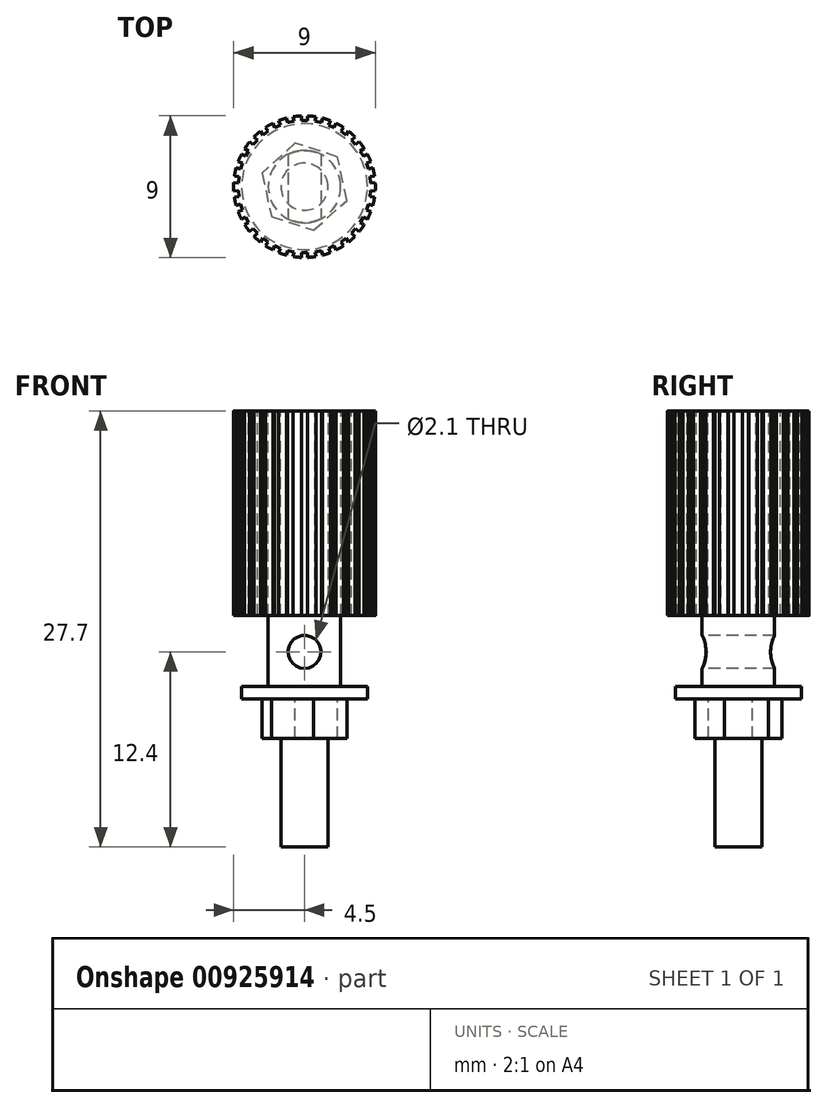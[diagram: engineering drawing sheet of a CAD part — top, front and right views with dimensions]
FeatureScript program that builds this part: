
annotation { "Feature Type Name" : "Feature", "Feature Type Description" : "" }
export const myFeature = defineFeature(function(context is Context, id is Id, definition is map)
    precondition{}
    {
        {
            var Q0;
            Q0=qCreatedBy(makeId("Top.planeOp"),FACE);
            var sketch = newSketch(context, id + "F0", { "sketchPlane" : qUnion([Q0])});
            skCircle(sketch, "E0", {"center": v(0, 0) * mm, "radius": 4 * mm});
            skSolve(sketch);
        }
        {
            var Q0;
            Q0 = qSketchRegion(id + "F0", true);
            extrude(context, id + "F1", {"entities" : qUnion([Q0]), "depth" : 0.8 * mm, "offsetDistance" : 25 * mm});
        }
        {
            var Q0;
            Q0=makeQuery(id+"F1.opExtrude","CAP_FACE",FACE,{"disambiguationData":[OSD([sQuery(id+"F0.wireOp",EDGE,"E0")])],"isStart":false});
            var sketch = newSketch(context, id + "F2", { "sketchPlane" : qUnion([Q0])});
            skCircle(sketch, "E1", {"center": v(0, 0) * mm, "radius": 2.3 * mm});
            skSolve(sketch);
        }
        {
            var Q0;
            Q0 = qSketchRegion(id + "F2", true);
            extrude(context, id + "F3", {"entities" : qUnion([Q0]), "operationType" : NewBodyOperationType.ADD, "depth" : 4.5 * mm, "offsetDistance" : 25 * mm});
        }
        {
            var Q0;
            Q0=makeQuery(id+"F3.opExtrude","CAP_FACE",FACE,{"disambiguationData":[OSD([sQuery(id+"F2.wireOp",EDGE,"E1")])],"isStart":false});
            var sketch = newSketch(context, id + "F4", { "sketchPlane" : qUnion([Q0])});
            skCircle(sketch, "E2", {"center": v(0, 0) * mm, "radius": 4.5 * mm});
            skSolve(sketch);
        }
        {
            var Q0;
            Q0 = qSketchRegion(id + "F4", true);
            extrude(context, id + "F5", {"entities" : qUnion([Q0]), "operationType" : NewBodyOperationType.ADD, "depth" : 13 * mm, "offsetDistance" : 25 * mm});
        }
        {
            var Q0;
            Q0=makeQuery(id+"F1.opExtrude","CAP_FACE",FACE,{"disambiguationData":[OSD([sQuery(id+"F0.wireOp",EDGE,"E0")])],"isStart":true});
            var sketch = newSketch(context, id + "F6", { "sketchPlane" : qUnion([Q0])});
            skCircle(sketch, "E3", {"center": v(0, 0) * mm, "radius": 1.5 * mm});
            skSolve(sketch);
        }
        {
            var Q0;
            Q0 = qSketchRegion(id + "F6", true);
            extrude(context, id + "F7", {"entities" : qUnion([Q0]), "operationType" : NewBodyOperationType.ADD, "depth" : 9.4 * mm, "offsetDistance" : 25 * mm});
        }
        {
            var Q0;
            Q0=qCreatedBy(makeId("Front.planeOp"),FACE);
            var sketch = newSketch(context, id + "F8", { "sketchPlane" : qUnion([Q0])});
            skCircle(sketch, "E4", {"center": v(0, 3) * mm, "radius": 1.05 * mm});
            skSolve(sketch);
        }
        {
            var Q0;
            Q0 = qSketchRegion(id + "F8", true);
            extrude(context, id + "F9", {"entities" : qUnion([Q0]), "operationType" : NewBodyOperationType.REMOVE, "oppositeDirection" : true, "depth" : 25 * mm, "offsetDistance" : 25 * mm, "symmetric" : true});
        }
        {
            var Q0;
            Q0=makeQuery(id+"F5.opExtrude","CAP_FACE",FACE,{"disambiguationData":[OSD([sQuery(id+"F4.wireOp",EDGE,"E2")])],"isStart":false});
            var sketch = newSketch(context, id + "F10", { "sketchPlane" : qUnion([Q0])});
            skLineSegment(sketch, "E5.bottom", {"start": v(0.2, 4.2) * mm, "end": v(-0.2, 4.2) * mm});
            skLineSegment(sketch, "E5.top", {"start": v(0.2, 4.8) * mm, "end": v(-0.2, 4.8) * mm});
            skLineSegment(sketch, "E5.left", {"start": v(0.2, 4.2) * mm, "end": v(0.2, 4.8) * mm});
            skLineSegment(sketch, "E5.right", {"start": v(-0.2, 4.2) * mm, "end": v(-0.2, 4.8) * mm});
            skPoint(sketch, "E5.middle", {"position": v(0, 4.5) * mm});
            skSolve(sketch);
        }
        {
            var Q0;
            Q0 = qSketchRegion(id + "F10", true);
            extrude(context, id + "F11", {"entities" : qUnion([Q0]), "oppositeDirection" : true, "depth" : 25 * mm, "offsetDistance" : 25 * mm});
        }
        {
            var Q0;
            Q0=makeQuery(id+"F11.opExtrude","SWEPT_BODY",BODY,{"disambiguationData":[OSD([sQuery(id+"F10.wireOp",EDGE,"E5.bottom"),sQuery(id+"F10.wireOp",EDGE,"E5.top"),sQuery(id+"F10.wireOp",EDGE,"E5.left"),sQuery(id+"F10.wireOp",EDGE,"E5.right")])]});
            var Q1;
            Q1=makeQuery(id+"F5.opExtrude","CAP_EDGE",EDGE,{"disambiguationData":[OSD([sQuery(id+"F4.wireOp",EDGE,"E2")])],"isStart":false});
            circularPattern(context, id + "F12", {"entities" : qUnion([Q0]), "axis" : qUnion([Q1]), "angle" : 360 * degree, "instanceCount" : 30, "equalSpace" : true});
        }
        {
            var Q0;
            Q0=makeQuery(id+"F12.opPattern","COPY",BODY,{"derivedFrom":makeQuery(id+"F11.opExtrude","SWEPT_BODY",BODY,{"disambiguationData":[OSD([sQuery(id+"F10.wireOp",EDGE,"E5.bottom"),sQuery(id+"F10.wireOp",EDGE,"E5.top"),sQuery(id+"F10.wireOp",EDGE,"E5.left"),sQuery(id+"F10.wireOp",EDGE,"E5.right")])]}),"instanceName":"1"});
            var Q1;
            Q1=makeQuery(id+"F12.opPattern","COPY",BODY,{"derivedFrom":makeQuery(id+"F11.opExtrude","SWEPT_BODY",BODY,{"disambiguationData":[OSD([sQuery(id+"F10.wireOp",EDGE,"E5.bottom"),sQuery(id+"F10.wireOp",EDGE,"E5.top"),sQuery(id+"F10.wireOp",EDGE,"E5.left"),sQuery(id+"F10.wireOp",EDGE,"E5.right")])]}),"instanceName":"2"});
            var Q2;
            Q2=makeQuery(id+"F12.opPattern","COPY",BODY,{"derivedFrom":makeQuery(id+"F11.opExtrude","SWEPT_BODY",BODY,{"disambiguationData":[OSD([sQuery(id+"F10.wireOp",EDGE,"E5.bottom"),sQuery(id+"F10.wireOp",EDGE,"E5.top"),sQuery(id+"F10.wireOp",EDGE,"E5.left"),sQuery(id+"F10.wireOp",EDGE,"E5.right")])]}),"instanceName":"3"});
            var Q3;
            Q3=makeQuery(id+"F12.opPattern","COPY",BODY,{"derivedFrom":makeQuery(id+"F11.opExtrude","SWEPT_BODY",BODY,{"disambiguationData":[OSD([sQuery(id+"F10.wireOp",EDGE,"E5.bottom"),sQuery(id+"F10.wireOp",EDGE,"E5.top"),sQuery(id+"F10.wireOp",EDGE,"E5.left"),sQuery(id+"F10.wireOp",EDGE,"E5.right")])]}),"instanceName":"4"});
            var Q4;
            Q4=makeQuery(id+"F12.opPattern","COPY",BODY,{"derivedFrom":makeQuery(id+"F11.opExtrude","SWEPT_BODY",BODY,{"disambiguationData":[OSD([sQuery(id+"F10.wireOp",EDGE,"E5.bottom"),sQuery(id+"F10.wireOp",EDGE,"E5.top"),sQuery(id+"F10.wireOp",EDGE,"E5.left"),sQuery(id+"F10.wireOp",EDGE,"E5.right")])]}),"instanceName":"5"});
            var Q5;
            Q5=makeQuery(id+"F12.opPattern","COPY",BODY,{"derivedFrom":makeQuery(id+"F11.opExtrude","SWEPT_BODY",BODY,{"disambiguationData":[OSD([sQuery(id+"F10.wireOp",EDGE,"E5.bottom"),sQuery(id+"F10.wireOp",EDGE,"E5.top"),sQuery(id+"F10.wireOp",EDGE,"E5.left"),sQuery(id+"F10.wireOp",EDGE,"E5.right")])]}),"instanceName":"6"});
            var Q6;
            Q6=makeQuery(id+"F12.opPattern","COPY",BODY,{"derivedFrom":makeQuery(id+"F11.opExtrude","SWEPT_BODY",BODY,{"disambiguationData":[OSD([sQuery(id+"F10.wireOp",EDGE,"E5.bottom"),sQuery(id+"F10.wireOp",EDGE,"E5.top"),sQuery(id+"F10.wireOp",EDGE,"E5.left"),sQuery(id+"F10.wireOp",EDGE,"E5.right")])]}),"instanceName":"7"});
            var Q7;
            Q7=makeQuery(id+"F12.opPattern","COPY",BODY,{"derivedFrom":makeQuery(id+"F11.opExtrude","SWEPT_BODY",BODY,{"disambiguationData":[OSD([sQuery(id+"F10.wireOp",EDGE,"E5.bottom"),sQuery(id+"F10.wireOp",EDGE,"E5.top"),sQuery(id+"F10.wireOp",EDGE,"E5.left"),sQuery(id+"F10.wireOp",EDGE,"E5.right")])]}),"instanceName":"8"});
            var Q8;
            Q8=makeQuery(id+"F12.opPattern","COPY",BODY,{"derivedFrom":makeQuery(id+"F11.opExtrude","SWEPT_BODY",BODY,{"disambiguationData":[OSD([sQuery(id+"F10.wireOp",EDGE,"E5.bottom"),sQuery(id+"F10.wireOp",EDGE,"E5.top"),sQuery(id+"F10.wireOp",EDGE,"E5.left"),sQuery(id+"F10.wireOp",EDGE,"E5.right")])]}),"instanceName":"9"});
            var Q9;
            Q9=makeQuery(id+"F12.opPattern","COPY",BODY,{"derivedFrom":makeQuery(id+"F11.opExtrude","SWEPT_BODY",BODY,{"disambiguationData":[OSD([sQuery(id+"F10.wireOp",EDGE,"E5.bottom"),sQuery(id+"F10.wireOp",EDGE,"E5.top"),sQuery(id+"F10.wireOp",EDGE,"E5.left"),sQuery(id+"F10.wireOp",EDGE,"E5.right")])]}),"instanceName":"10"});
            var Q10;
            Q10=makeQuery(id+"F12.opPattern","COPY",BODY,{"derivedFrom":makeQuery(id+"F11.opExtrude","SWEPT_BODY",BODY,{"disambiguationData":[OSD([sQuery(id+"F10.wireOp",EDGE,"E5.bottom"),sQuery(id+"F10.wireOp",EDGE,"E5.top"),sQuery(id+"F10.wireOp",EDGE,"E5.left"),sQuery(id+"F10.wireOp",EDGE,"E5.right")])]}),"instanceName":"11"});
            var Q11;
            Q11=makeQuery(id+"F12.opPattern","COPY",BODY,{"derivedFrom":makeQuery(id+"F11.opExtrude","SWEPT_BODY",BODY,{"disambiguationData":[OSD([sQuery(id+"F10.wireOp",EDGE,"E5.bottom"),sQuery(id+"F10.wireOp",EDGE,"E5.top"),sQuery(id+"F10.wireOp",EDGE,"E5.left"),sQuery(id+"F10.wireOp",EDGE,"E5.right")])]}),"instanceName":"12"});
            var Q12;
            Q12=makeQuery(id+"F12.opPattern","COPY",BODY,{"derivedFrom":makeQuery(id+"F11.opExtrude","SWEPT_BODY",BODY,{"disambiguationData":[OSD([sQuery(id+"F10.wireOp",EDGE,"E5.bottom"),sQuery(id+"F10.wireOp",EDGE,"E5.top"),sQuery(id+"F10.wireOp",EDGE,"E5.left"),sQuery(id+"F10.wireOp",EDGE,"E5.right")])]}),"instanceName":"13"});
            var Q13;
            Q13=makeQuery(id+"F12.opPattern","COPY",BODY,{"derivedFrom":makeQuery(id+"F11.opExtrude","SWEPT_BODY",BODY,{"disambiguationData":[OSD([sQuery(id+"F10.wireOp",EDGE,"E5.bottom"),sQuery(id+"F10.wireOp",EDGE,"E5.top"),sQuery(id+"F10.wireOp",EDGE,"E5.left"),sQuery(id+"F10.wireOp",EDGE,"E5.right")])]}),"instanceName":"14"});
            var Q14;
            Q14=makeQuery(id+"F12.opPattern","COPY",BODY,{"derivedFrom":makeQuery(id+"F11.opExtrude","SWEPT_BODY",BODY,{"disambiguationData":[OSD([sQuery(id+"F10.wireOp",EDGE,"E5.bottom"),sQuery(id+"F10.wireOp",EDGE,"E5.top"),sQuery(id+"F10.wireOp",EDGE,"E5.left"),sQuery(id+"F10.wireOp",EDGE,"E5.right")])]}),"instanceName":"15"});
            var Q15;
            Q15=makeQuery(id+"F12.opPattern","COPY",BODY,{"derivedFrom":makeQuery(id+"F11.opExtrude","SWEPT_BODY",BODY,{"disambiguationData":[OSD([sQuery(id+"F10.wireOp",EDGE,"E5.bottom"),sQuery(id+"F10.wireOp",EDGE,"E5.top"),sQuery(id+"F10.wireOp",EDGE,"E5.left"),sQuery(id+"F10.wireOp",EDGE,"E5.right")])]}),"instanceName":"16"});
            var Q16;
            Q16=makeQuery(id+"F12.opPattern","COPY",BODY,{"derivedFrom":makeQuery(id+"F11.opExtrude","SWEPT_BODY",BODY,{"disambiguationData":[OSD([sQuery(id+"F10.wireOp",EDGE,"E5.bottom"),sQuery(id+"F10.wireOp",EDGE,"E5.top"),sQuery(id+"F10.wireOp",EDGE,"E5.left"),sQuery(id+"F10.wireOp",EDGE,"E5.right")])]}),"instanceName":"17"});
            var Q17;
            Q17=makeQuery(id+"F12.opPattern","COPY",BODY,{"derivedFrom":makeQuery(id+"F11.opExtrude","SWEPT_BODY",BODY,{"disambiguationData":[OSD([sQuery(id+"F10.wireOp",EDGE,"E5.bottom"),sQuery(id+"F10.wireOp",EDGE,"E5.top"),sQuery(id+"F10.wireOp",EDGE,"E5.left"),sQuery(id+"F10.wireOp",EDGE,"E5.right")])]}),"instanceName":"18"});
            var Q18;
            Q18=makeQuery(id+"F12.opPattern","COPY",BODY,{"derivedFrom":makeQuery(id+"F11.opExtrude","SWEPT_BODY",BODY,{"disambiguationData":[OSD([sQuery(id+"F10.wireOp",EDGE,"E5.bottom"),sQuery(id+"F10.wireOp",EDGE,"E5.top"),sQuery(id+"F10.wireOp",EDGE,"E5.left"),sQuery(id+"F10.wireOp",EDGE,"E5.right")])]}),"instanceName":"19"});
            var Q19;
            Q19=makeQuery(id+"F12.opPattern","COPY",BODY,{"derivedFrom":makeQuery(id+"F11.opExtrude","SWEPT_BODY",BODY,{"disambiguationData":[OSD([sQuery(id+"F10.wireOp",EDGE,"E5.bottom"),sQuery(id+"F10.wireOp",EDGE,"E5.top"),sQuery(id+"F10.wireOp",EDGE,"E5.left"),sQuery(id+"F10.wireOp",EDGE,"E5.right")])]}),"instanceName":"20"});
            var Q20;
            Q20=makeQuery(id+"F12.opPattern","COPY",BODY,{"derivedFrom":makeQuery(id+"F11.opExtrude","SWEPT_BODY",BODY,{"disambiguationData":[OSD([sQuery(id+"F10.wireOp",EDGE,"E5.bottom"),sQuery(id+"F10.wireOp",EDGE,"E5.top"),sQuery(id+"F10.wireOp",EDGE,"E5.left"),sQuery(id+"F10.wireOp",EDGE,"E5.right")])]}),"instanceName":"21"});
            var Q21;
            Q21=makeQuery(id+"F12.opPattern","COPY",BODY,{"derivedFrom":makeQuery(id+"F11.opExtrude","SWEPT_BODY",BODY,{"disambiguationData":[OSD([sQuery(id+"F10.wireOp",EDGE,"E5.bottom"),sQuery(id+"F10.wireOp",EDGE,"E5.top"),sQuery(id+"F10.wireOp",EDGE,"E5.left"),sQuery(id+"F10.wireOp",EDGE,"E5.right")])]}),"instanceName":"22"});
            var Q22;
            Q22=makeQuery(id+"F12.opPattern","COPY",BODY,{"derivedFrom":makeQuery(id+"F11.opExtrude","SWEPT_BODY",BODY,{"disambiguationData":[OSD([sQuery(id+"F10.wireOp",EDGE,"E5.bottom"),sQuery(id+"F10.wireOp",EDGE,"E5.top"),sQuery(id+"F10.wireOp",EDGE,"E5.left"),sQuery(id+"F10.wireOp",EDGE,"E5.right")])]}),"instanceName":"23"});
            var Q23;
            Q23=makeQuery(id+"F12.opPattern","COPY",BODY,{"derivedFrom":makeQuery(id+"F11.opExtrude","SWEPT_BODY",BODY,{"disambiguationData":[OSD([sQuery(id+"F10.wireOp",EDGE,"E5.bottom"),sQuery(id+"F10.wireOp",EDGE,"E5.top"),sQuery(id+"F10.wireOp",EDGE,"E5.left"),sQuery(id+"F10.wireOp",EDGE,"E5.right")])]}),"instanceName":"24"});
            var Q24;
            Q24=makeQuery(id+"F12.opPattern","COPY",BODY,{"derivedFrom":makeQuery(id+"F11.opExtrude","SWEPT_BODY",BODY,{"disambiguationData":[OSD([sQuery(id+"F10.wireOp",EDGE,"E5.bottom"),sQuery(id+"F10.wireOp",EDGE,"E5.top"),sQuery(id+"F10.wireOp",EDGE,"E5.left"),sQuery(id+"F10.wireOp",EDGE,"E5.right")])]}),"instanceName":"25"});
            var Q25;
            Q25=makeQuery(id+"F12.opPattern","COPY",BODY,{"derivedFrom":makeQuery(id+"F11.opExtrude","SWEPT_BODY",BODY,{"disambiguationData":[OSD([sQuery(id+"F10.wireOp",EDGE,"E5.bottom"),sQuery(id+"F10.wireOp",EDGE,"E5.top"),sQuery(id+"F10.wireOp",EDGE,"E5.left"),sQuery(id+"F10.wireOp",EDGE,"E5.right")])]}),"instanceName":"26"});
            var Q26;
            Q26=makeQuery(id+"F12.opPattern","COPY",BODY,{"derivedFrom":makeQuery(id+"F11.opExtrude","SWEPT_BODY",BODY,{"disambiguationData":[OSD([sQuery(id+"F10.wireOp",EDGE,"E5.bottom"),sQuery(id+"F10.wireOp",EDGE,"E5.top"),sQuery(id+"F10.wireOp",EDGE,"E5.left"),sQuery(id+"F10.wireOp",EDGE,"E5.right")])]}),"instanceName":"27"});
            var Q27;
            Q27=makeQuery(id+"F12.opPattern","COPY",BODY,{"derivedFrom":makeQuery(id+"F11.opExtrude","SWEPT_BODY",BODY,{"disambiguationData":[OSD([sQuery(id+"F10.wireOp",EDGE,"E5.bottom"),sQuery(id+"F10.wireOp",EDGE,"E5.top"),sQuery(id+"F10.wireOp",EDGE,"E5.left"),sQuery(id+"F10.wireOp",EDGE,"E5.right")])]}),"instanceName":"28"});
            var Q28;
            Q28=makeQuery(id+"F12.opPattern","COPY",BODY,{"derivedFrom":makeQuery(id+"F11.opExtrude","SWEPT_BODY",BODY,{"disambiguationData":[OSD([sQuery(id+"F10.wireOp",EDGE,"E5.bottom"),sQuery(id+"F10.wireOp",EDGE,"E5.top"),sQuery(id+"F10.wireOp",EDGE,"E5.left"),sQuery(id+"F10.wireOp",EDGE,"E5.right")])]}),"instanceName":"29"});
            var Q29;
            Q29=makeQuery(id+"F12.opPattern","COPY",BODY,{"derivedFrom":makeQuery(id+"F11.opExtrude","SWEPT_BODY",BODY,{"disambiguationData":[OSD([sQuery(id+"F10.wireOp",EDGE,"E5.bottom"),sQuery(id+"F10.wireOp",EDGE,"E5.top"),sQuery(id+"F10.wireOp",EDGE,"E5.left"),sQuery(id+"F10.wireOp",EDGE,"E5.right")])]}),"instanceName":"30"});
            var Q30;
            Q30=makeQuery(id+"F12.opPattern","COPY",BODY,{"derivedFrom":makeQuery(id+"F11.opExtrude","SWEPT_BODY",BODY,{"disambiguationData":[OSD([sQuery(id+"F10.wireOp",EDGE,"E5.bottom"),sQuery(id+"F10.wireOp",EDGE,"E5.top"),sQuery(id+"F10.wireOp",EDGE,"E5.left"),sQuery(id+"F10.wireOp",EDGE,"E5.right")])]}),"instanceName":"31"});
            var Q31;
            Q31=makeQuery(id+"F12.opPattern","COPY",BODY,{"derivedFrom":makeQuery(id+"F11.opExtrude","SWEPT_BODY",BODY,{"disambiguationData":[OSD([sQuery(id+"F10.wireOp",EDGE,"E5.bottom"),sQuery(id+"F10.wireOp",EDGE,"E5.top"),sQuery(id+"F10.wireOp",EDGE,"E5.left"),sQuery(id+"F10.wireOp",EDGE,"E5.right")])]}),"instanceName":"32"});
            var Q32;
            Q32=makeQuery(id+"F12.opPattern","COPY",BODY,{"derivedFrom":makeQuery(id+"F11.opExtrude","SWEPT_BODY",BODY,{"disambiguationData":[OSD([sQuery(id+"F10.wireOp",EDGE,"E5.bottom"),sQuery(id+"F10.wireOp",EDGE,"E5.top"),sQuery(id+"F10.wireOp",EDGE,"E5.left"),sQuery(id+"F10.wireOp",EDGE,"E5.right")])]}),"instanceName":"33"});
            var Q33;
            Q33=makeQuery(id+"F12.opPattern","COPY",BODY,{"derivedFrom":makeQuery(id+"F11.opExtrude","SWEPT_BODY",BODY,{"disambiguationData":[OSD([sQuery(id+"F10.wireOp",EDGE,"E5.bottom"),sQuery(id+"F10.wireOp",EDGE,"E5.top"),sQuery(id+"F10.wireOp",EDGE,"E5.left"),sQuery(id+"F10.wireOp",EDGE,"E5.right")])]}),"instanceName":"34"});
            var Q34;
            Q34=makeQuery(id+"F12.opPattern","COPY",BODY,{"derivedFrom":makeQuery(id+"F11.opExtrude","SWEPT_BODY",BODY,{"disambiguationData":[OSD([sQuery(id+"F10.wireOp",EDGE,"E5.bottom"),sQuery(id+"F10.wireOp",EDGE,"E5.top"),sQuery(id+"F10.wireOp",EDGE,"E5.left"),sQuery(id+"F10.wireOp",EDGE,"E5.right")])]}),"instanceName":"35"});
            var Q35;
            Q35=makeQuery(id+"F12.opPattern","COPY",BODY,{"derivedFrom":makeQuery(id+"F11.opExtrude","SWEPT_BODY",BODY,{"disambiguationData":[OSD([sQuery(id+"F10.wireOp",EDGE,"E5.bottom"),sQuery(id+"F10.wireOp",EDGE,"E5.top"),sQuery(id+"F10.wireOp",EDGE,"E5.left"),sQuery(id+"F10.wireOp",EDGE,"E5.right")])]}),"instanceName":"36"});
            var Q36;
            Q36=makeQuery(id+"F12.opPattern","COPY",BODY,{"derivedFrom":makeQuery(id+"F11.opExtrude","SWEPT_BODY",BODY,{"disambiguationData":[OSD([sQuery(id+"F10.wireOp",EDGE,"E5.bottom"),sQuery(id+"F10.wireOp",EDGE,"E5.top"),sQuery(id+"F10.wireOp",EDGE,"E5.left"),sQuery(id+"F10.wireOp",EDGE,"E5.right")])]}),"instanceName":"37"});
            var Q37;
            Q37=makeQuery(id+"F12.opPattern","COPY",BODY,{"derivedFrom":makeQuery(id+"F11.opExtrude","SWEPT_BODY",BODY,{"disambiguationData":[OSD([sQuery(id+"F10.wireOp",EDGE,"E5.bottom"),sQuery(id+"F10.wireOp",EDGE,"E5.top"),sQuery(id+"F10.wireOp",EDGE,"E5.left"),sQuery(id+"F10.wireOp",EDGE,"E5.right")])]}),"instanceName":"38"});
            var Q38;
            Q38=makeQuery(id+"F12.opPattern","COPY",BODY,{"derivedFrom":makeQuery(id+"F11.opExtrude","SWEPT_BODY",BODY,{"disambiguationData":[OSD([sQuery(id+"F10.wireOp",EDGE,"E5.bottom"),sQuery(id+"F10.wireOp",EDGE,"E5.top"),sQuery(id+"F10.wireOp",EDGE,"E5.left"),sQuery(id+"F10.wireOp",EDGE,"E5.right")])]}),"instanceName":"39"});
            var Q39;
            Q39=makeQuery(id+"F12.opPattern","COPY",BODY,{"derivedFrom":makeQuery(id+"F11.opExtrude","SWEPT_BODY",BODY,{"disambiguationData":[OSD([sQuery(id+"F10.wireOp",EDGE,"E5.bottom"),sQuery(id+"F10.wireOp",EDGE,"E5.top"),sQuery(id+"F10.wireOp",EDGE,"E5.left"),sQuery(id+"F10.wireOp",EDGE,"E5.right")])]}),"instanceName":"40"});
            var Q40;
            Q40=makeQuery(id+"F12.opPattern","COPY",BODY,{"derivedFrom":makeQuery(id+"F11.opExtrude","SWEPT_BODY",BODY,{"disambiguationData":[OSD([sQuery(id+"F10.wireOp",EDGE,"E5.bottom"),sQuery(id+"F10.wireOp",EDGE,"E5.top"),sQuery(id+"F10.wireOp",EDGE,"E5.left"),sQuery(id+"F10.wireOp",EDGE,"E5.right")])]}),"instanceName":"41"});
            var Q41;
            Q41=makeQuery(id+"F12.opPattern","COPY",BODY,{"derivedFrom":makeQuery(id+"F11.opExtrude","SWEPT_BODY",BODY,{"disambiguationData":[OSD([sQuery(id+"F10.wireOp",EDGE,"E5.bottom"),sQuery(id+"F10.wireOp",EDGE,"E5.top"),sQuery(id+"F10.wireOp",EDGE,"E5.left"),sQuery(id+"F10.wireOp",EDGE,"E5.right")])]}),"instanceName":"42"});
            var Q42;
            Q42=makeQuery(id+"F12.opPattern","COPY",BODY,{"derivedFrom":makeQuery(id+"F11.opExtrude","SWEPT_BODY",BODY,{"disambiguationData":[OSD([sQuery(id+"F10.wireOp",EDGE,"E5.bottom"),sQuery(id+"F10.wireOp",EDGE,"E5.top"),sQuery(id+"F10.wireOp",EDGE,"E5.left"),sQuery(id+"F10.wireOp",EDGE,"E5.right")])]}),"instanceName":"43"});
            var Q43;
            Q43=makeQuery(id+"F12.opPattern","COPY",BODY,{"derivedFrom":makeQuery(id+"F11.opExtrude","SWEPT_BODY",BODY,{"disambiguationData":[OSD([sQuery(id+"F10.wireOp",EDGE,"E5.bottom"),sQuery(id+"F10.wireOp",EDGE,"E5.top"),sQuery(id+"F10.wireOp",EDGE,"E5.left"),sQuery(id+"F10.wireOp",EDGE,"E5.right")])]}),"instanceName":"44"});
            var Q44;
            Q44=makeQuery(id+"F12.opPattern","COPY",BODY,{"derivedFrom":makeQuery(id+"F11.opExtrude","SWEPT_BODY",BODY,{"disambiguationData":[OSD([sQuery(id+"F10.wireOp",EDGE,"E5.bottom"),sQuery(id+"F10.wireOp",EDGE,"E5.top"),sQuery(id+"F10.wireOp",EDGE,"E5.left"),sQuery(id+"F10.wireOp",EDGE,"E5.right")])]}),"instanceName":"45"});
            var Q45;
            Q45=makeQuery(id+"F12.opPattern","COPY",BODY,{"derivedFrom":makeQuery(id+"F11.opExtrude","SWEPT_BODY",BODY,{"disambiguationData":[OSD([sQuery(id+"F10.wireOp",EDGE,"E5.bottom"),sQuery(id+"F10.wireOp",EDGE,"E5.top"),sQuery(id+"F10.wireOp",EDGE,"E5.left"),sQuery(id+"F10.wireOp",EDGE,"E5.right")])]}),"instanceName":"46"});
            var Q46;
            Q46=makeQuery(id+"F12.opPattern","COPY",BODY,{"derivedFrom":makeQuery(id+"F11.opExtrude","SWEPT_BODY",BODY,{"disambiguationData":[OSD([sQuery(id+"F10.wireOp",EDGE,"E5.bottom"),sQuery(id+"F10.wireOp",EDGE,"E5.top"),sQuery(id+"F10.wireOp",EDGE,"E5.left"),sQuery(id+"F10.wireOp",EDGE,"E5.right")])]}),"instanceName":"47"});
            var Q47;
            Q47=makeQuery(id+"F12.opPattern","COPY",BODY,{"derivedFrom":makeQuery(id+"F11.opExtrude","SWEPT_BODY",BODY,{"disambiguationData":[OSD([sQuery(id+"F10.wireOp",EDGE,"E5.bottom"),sQuery(id+"F10.wireOp",EDGE,"E5.top"),sQuery(id+"F10.wireOp",EDGE,"E5.left"),sQuery(id+"F10.wireOp",EDGE,"E5.right")])]}),"instanceName":"48"});
            var Q48;
            Q48=makeQuery(id+"F12.opPattern","COPY",BODY,{"derivedFrom":makeQuery(id+"F11.opExtrude","SWEPT_BODY",BODY,{"disambiguationData":[OSD([sQuery(id+"F10.wireOp",EDGE,"E5.bottom"),sQuery(id+"F10.wireOp",EDGE,"E5.top"),sQuery(id+"F10.wireOp",EDGE,"E5.left"),sQuery(id+"F10.wireOp",EDGE,"E5.right")])]}),"instanceName":"49"});
            var Q49;
            Q49=makeQuery(id+"F12.opPattern","COPY",BODY,{"derivedFrom":makeQuery(id+"F11.opExtrude","SWEPT_BODY",BODY,{"disambiguationData":[OSD([sQuery(id+"F10.wireOp",EDGE,"E5.bottom"),sQuery(id+"F10.wireOp",EDGE,"E5.top"),sQuery(id+"F10.wireOp",EDGE,"E5.left"),sQuery(id+"F10.wireOp",EDGE,"E5.right")])]}),"instanceName":"50"});
            var Q50;
            Q50=makeQuery(id+"F12.opPattern","COPY",BODY,{"derivedFrom":makeQuery(id+"F11.opExtrude","SWEPT_BODY",BODY,{"disambiguationData":[OSD([sQuery(id+"F10.wireOp",EDGE,"E5.bottom"),sQuery(id+"F10.wireOp",EDGE,"E5.top"),sQuery(id+"F10.wireOp",EDGE,"E5.left"),sQuery(id+"F10.wireOp",EDGE,"E5.right")])]}),"instanceName":"51"});
            var Q51;
            Q51=makeQuery(id+"F12.opPattern","COPY",BODY,{"derivedFrom":makeQuery(id+"F11.opExtrude","SWEPT_BODY",BODY,{"disambiguationData":[OSD([sQuery(id+"F10.wireOp",EDGE,"E5.bottom"),sQuery(id+"F10.wireOp",EDGE,"E5.top"),sQuery(id+"F10.wireOp",EDGE,"E5.left"),sQuery(id+"F10.wireOp",EDGE,"E5.right")])]}),"instanceName":"52"});
            var Q52;
            Q52=makeQuery(id+"F12.opPattern","COPY",BODY,{"derivedFrom":makeQuery(id+"F11.opExtrude","SWEPT_BODY",BODY,{"disambiguationData":[OSD([sQuery(id+"F10.wireOp",EDGE,"E5.bottom"),sQuery(id+"F10.wireOp",EDGE,"E5.top"),sQuery(id+"F10.wireOp",EDGE,"E5.left"),sQuery(id+"F10.wireOp",EDGE,"E5.right")])]}),"instanceName":"53"});
            var Q53;
            Q53=makeQuery(id+"F12.opPattern","COPY",BODY,{"derivedFrom":makeQuery(id+"F11.opExtrude","SWEPT_BODY",BODY,{"disambiguationData":[OSD([sQuery(id+"F10.wireOp",EDGE,"E5.bottom"),sQuery(id+"F10.wireOp",EDGE,"E5.top"),sQuery(id+"F10.wireOp",EDGE,"E5.left"),sQuery(id+"F10.wireOp",EDGE,"E5.right")])]}),"instanceName":"54"});
            var Q54;
            Q54=makeQuery(id+"F12.opPattern","COPY",BODY,{"derivedFrom":makeQuery(id+"F11.opExtrude","SWEPT_BODY",BODY,{"disambiguationData":[OSD([sQuery(id+"F10.wireOp",EDGE,"E5.bottom"),sQuery(id+"F10.wireOp",EDGE,"E5.top"),sQuery(id+"F10.wireOp",EDGE,"E5.left"),sQuery(id+"F10.wireOp",EDGE,"E5.right")])]}),"instanceName":"55"});
            var Q55;
            Q55=makeQuery(id+"F12.opPattern","COPY",BODY,{"derivedFrom":makeQuery(id+"F11.opExtrude","SWEPT_BODY",BODY,{"disambiguationData":[OSD([sQuery(id+"F10.wireOp",EDGE,"E5.bottom"),sQuery(id+"F10.wireOp",EDGE,"E5.top"),sQuery(id+"F10.wireOp",EDGE,"E5.left"),sQuery(id+"F10.wireOp",EDGE,"E5.right")])]}),"instanceName":"56"});
            var Q56;
            Q56=makeQuery(id+"F12.opPattern","COPY",BODY,{"derivedFrom":makeQuery(id+"F11.opExtrude","SWEPT_BODY",BODY,{"disambiguationData":[OSD([sQuery(id+"F10.wireOp",EDGE,"E5.bottom"),sQuery(id+"F10.wireOp",EDGE,"E5.top"),sQuery(id+"F10.wireOp",EDGE,"E5.left"),sQuery(id+"F10.wireOp",EDGE,"E5.right")])]}),"instanceName":"57"});
            var Q57;
            Q57=makeQuery(id+"F12.opPattern","COPY",BODY,{"derivedFrom":makeQuery(id+"F11.opExtrude","SWEPT_BODY",BODY,{"disambiguationData":[OSD([sQuery(id+"F10.wireOp",EDGE,"E5.bottom"),sQuery(id+"F10.wireOp",EDGE,"E5.top"),sQuery(id+"F10.wireOp",EDGE,"E5.left"),sQuery(id+"F10.wireOp",EDGE,"E5.right")])]}),"instanceName":"58"});
            var Q58;
            Q58=makeQuery(id+"F12.opPattern","COPY",BODY,{"derivedFrom":makeQuery(id+"F11.opExtrude","SWEPT_BODY",BODY,{"disambiguationData":[OSD([sQuery(id+"F10.wireOp",EDGE,"E5.bottom"),sQuery(id+"F10.wireOp",EDGE,"E5.top"),sQuery(id+"F10.wireOp",EDGE,"E5.left"),sQuery(id+"F10.wireOp",EDGE,"E5.right")])]}),"instanceName":"59"});
            var Q59;
            Q59=makeQuery(id+"F11.opExtrude","SWEPT_BODY",BODY,{"disambiguationData":[OSD([sQuery(id+"F10.wireOp",EDGE,"E5.bottom"),sQuery(id+"F10.wireOp",EDGE,"E5.top"),sQuery(id+"F10.wireOp",EDGE,"E5.left"),sQuery(id+"F10.wireOp",EDGE,"E5.right")])]});
            var Q60;
            Q60=makeQuery(id+"F1.opExtrude","SWEPT_BODY",BODY,{"disambiguationData":[OSD([sQuery(id+"F0.wireOp",EDGE,"E0")])]});
            booleanBodies(context, id + "F13", {"operationType" : BooleanOperationType.SUBTRACTION, "tools" : qUnion([Q0, Q1, Q2, Q3, Q4, Q5, Q6, Q7, Q8, Q9, Q10, Q11, Q12, Q13, Q14, Q15, Q16, Q17, Q18, Q19, Q20, Q21, Q22, Q23, Q24, Q25, Q26, Q27, Q28, Q29, Q30, Q31, Q32, Q33, Q34, Q35, Q36, Q37, Q38, Q39, Q40, Q41, Q42, Q43, Q44, Q45, Q46, Q47, Q48, Q49, Q50, Q51, Q52, Q53, Q54, Q55, Q56, Q57, Q58, Q59]), "targets" : qUnion([Q60])});
        }
        {
            var Q0;
            Q0=makeQuery(id+"F1.opExtrude","CAP_FACE",FACE,{"disambiguationData":[OSD([sQuery(id+"F0.wireOp",EDGE,"E0")])],"isStart":true});
            var sketch = newSketch(context, id + "F14", { "sketchPlane" : qUnion([Q0])});
            skCircle(sketch, "E6.cCircle", {"center": v(0, 0) * mm, "radius": 2.83 * mm, "construction": true});
            skLineSegment(sketch, "E6.0", {"start": v(-0.59, -2.77) * mm, "end": v(-2.7, -0.88) * mm});
            skLineSegment(sketch, "E6.1", {"start": v(-2.7, -0.88) * mm, "end": v(-2.1, 1.9) * mm});
            skLineSegment(sketch, "E6.2", {"start": v(-2.1, 1.9) * mm, "end": v(0.59, 2.77) * mm});
            skLineSegment(sketch, "E6.3", {"start": v(0.59, 2.77) * mm, "end": v(2.7, 0.88) * mm});
            skLineSegment(sketch, "E6.4", {"start": v(2.7, 0.88) * mm, "end": v(2.1, -1.9) * mm});
            skLineSegment(sketch, "E6.5", {"start": v(2.1, -1.9) * mm, "end": v(-0.59, -2.77) * mm});
            skSolve(sketch);
        }
        {
            var Q0;
            Q0 = qSketchRegion(id + "F14", true);
            extrude(context, id + "F15", {"entities" : qUnion([Q0]), "operationType" : NewBodyOperationType.ADD, "depth" : 2.5 * mm, "offsetDistance" : 25 * mm});
        }
    });
